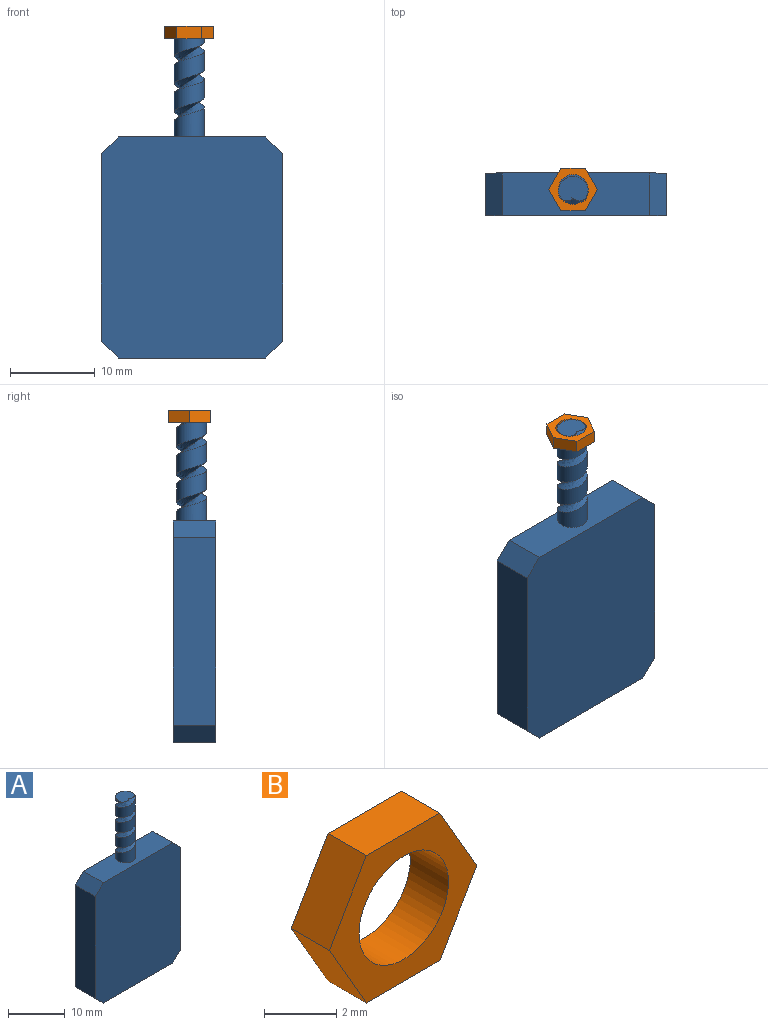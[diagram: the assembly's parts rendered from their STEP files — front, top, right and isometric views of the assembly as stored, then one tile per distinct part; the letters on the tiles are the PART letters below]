
ASSEMBLY  parts=2 mates=1
PART A: 19 faces, bbox 21.5x5.2x40.1 mm
  f0: cylinder r=1.75mm len=3.54mm, axis (0,0,-1), area 21mm2, adj f3,f7,f12,f13
  f1: cylinder r=1.75mm len=5.17mm, axis (0,0,-1), area 23.8mm2, adj f2,f4,f11,f13,f14
  f2: cylinder r=1.75mm len=5.44mm, axis (0,0,-1), area 23.9mm2, adj f1,f3,f13,f14
  f3: cylinder r=1.75mm len=5.44mm, axis (0,0,-1), area 23.9mm2, adj f0,f2,f13,f14
  f4: cylinder r=1.75mm len=3.51mm, axis (0,0,-1), area 6.1mm2, adj f1,f11,f14
  f5: plane 17.33x5mm, normal (0,0,-1), area 86.6mm2, adj f9,f10,f17,f18
  f6: plane 22.04x5mm, normal (1,0,0), area 110.2mm2, adj f9,f10,f16,f18
  f7: plane 17.33x5mm, normal (0,0,1), area 77mm2, adj f0,f9,f10,f15,f16
  f8: plane 22.04x5mm, normal (-1,0,0), area 110.2mm2, adj f9,f10,f15,f17
  f9: plane 26.04x21.33mm, normal (0,-1,0), area 547.4mm2, adj f5,f6,f7,f8,f15,f16,f17,f18
  f10: plane 26.04x21.33mm, normal (0,1,0), area 547.4mm2, adj f5,f6,f7,f8,f15,f16,f17,f18
  f11: plane 3.71x3.06mm, normal (0,0,1), area 8.2mm2, adj f1,f4,f13,f14
  f12: plane 1.1x0.95mm, normal (0,1,0), area 0.5mm2, adj f0,f13,f14
  f13: bspline ~13.36x3.5mm, area 36.1mm2, adj f0,f1,f2,f3,f11,f12,f14
  f14: bspline ~13.08x4.05mm, area 34.3mm2, adj f1,f2,f3,f4,f11,f12,f13
  f15: plane 5x2mm, normal (-0.71,0,0.71), area 14.1mm2, adj f7,f8,f9,f10
  f16: plane 5x2mm, normal (0.71,0,0.71), area 14.1mm2, adj f6,f7,f9,f10
  f17: plane 5x2mm, normal (-0.71,0,-0.71), area 14.1mm2, adj f5,f8,f9,f10
  f18: plane 5x2mm, normal (0.71,0,-0.71), area 14.1mm2, adj f5,f6,f9,f10
PART B: 9 faces, bbox 5.8x1.5x5 mm
  f0: plane 2.89x1.5mm, normal (0,0,1), area 4.3mm2, adj f1,f5,f6,f7
  f1: plane 2.5x1.5mm, normal (-0.87,0,0.5), area 4.3mm2, adj f0,f2,f6,f7
  f2: plane 2.5x1.5mm, normal (-0.87,0,-0.5), area 4.3mm2, adj f1,f3,f6,f7
  f3: plane 2.89x1.5mm, normal (0,0,-1), area 4.3mm2, adj f2,f4,f6,f7
  f4: plane 2.5x1.5mm, normal (0.87,0,-0.5), area 4.3mm2, adj f3,f5,f6,f7
  f5: plane 2.5x1.5mm, normal (0.87,0,0.5), area 4.3mm2, adj f0,f4,f6,f7
  f6: plane 5.77x5mm, normal (0,-1,0), area 12mm2, adj f0,f1,f2,f3,f4,f5,f8
  f7: plane 5.77x5mm, normal (0,1,0), area 12mm2, adj f0,f1,f2,f3,f4,f5,f8
  f8: cylinder r=1.75mm len=3.51mm, axis (0,1,0), area 16.5mm2, adj f6,f7
PLACE A t=(-7.16,3.2,-5.08)mm
PLACE B rot(axis=(1,0,0),90deg) t=(14.3,1.24,29.92)mm
MATE fastened B.f8 <-> A.f11  axis (0,0,1) through (-7.16,1.24,29.92)mm
